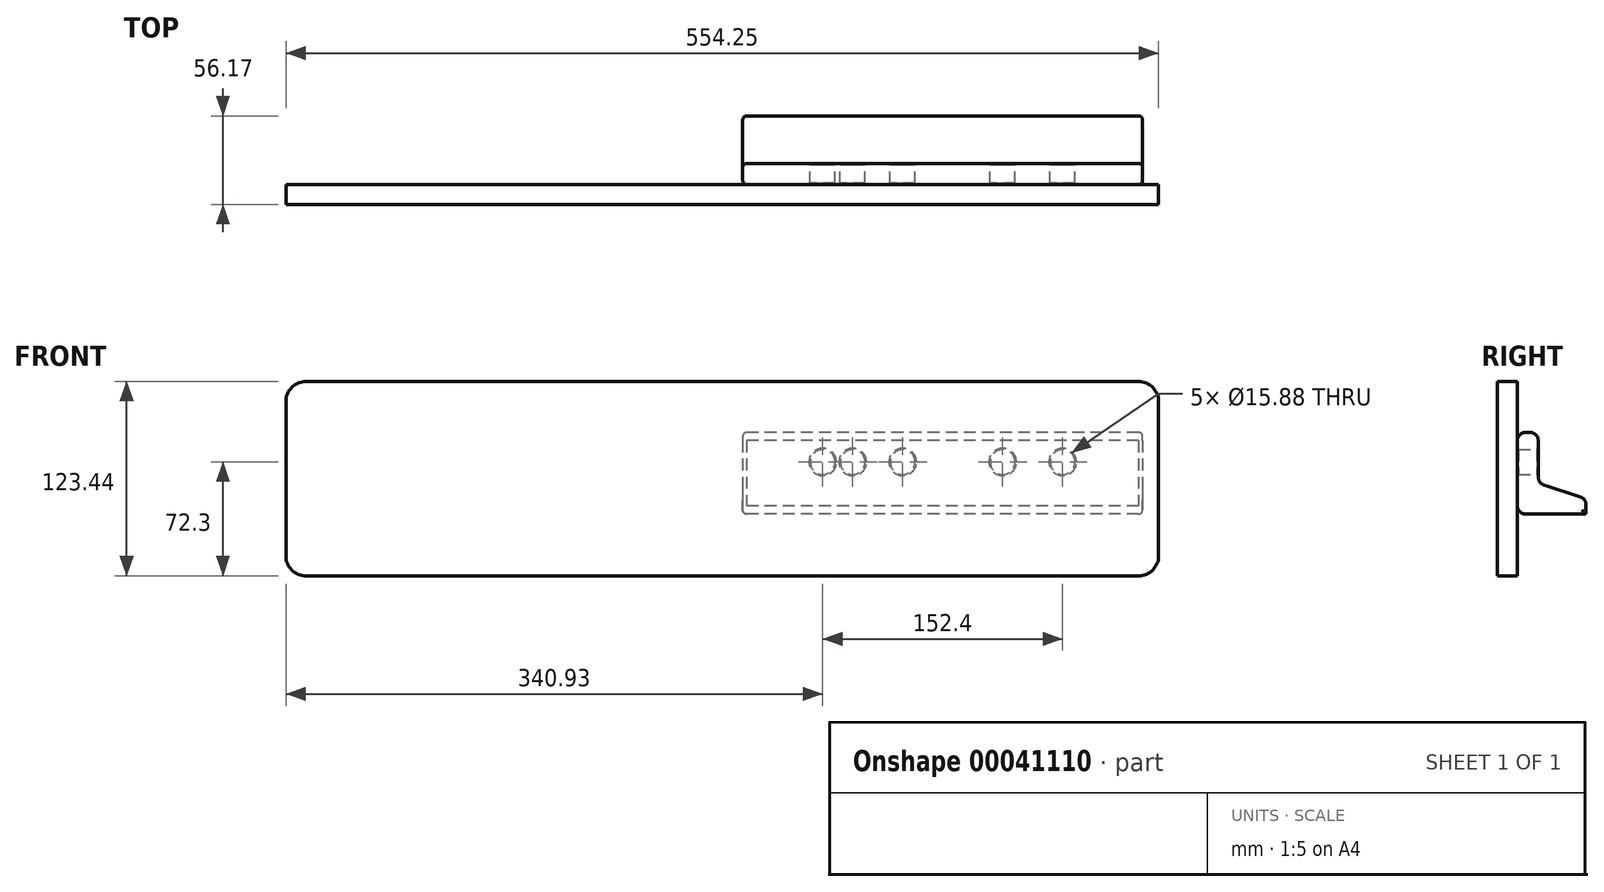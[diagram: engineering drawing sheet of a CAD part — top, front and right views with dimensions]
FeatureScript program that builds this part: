
annotation { "Feature Type Name" : "Feature", "Feature Type Description" : "" }
export const myFeature = defineFeature(function(context is Context, id is Id, definition is map)
    precondition{}
    {
        {
            var Q0;
            Q0=qCreatedBy(makeId("Right.planeOp"),FACE);
            var sketch = newSketch(context, id + "F0", { "sketchPlane" : qUnion([Q0])});
            skLineSegment(sketch, "E0.bottom", {"start": v(0, 51.75) * mm, "end": v(13.23, 51.75) * mm});
            skLineSegment(sketch, "E0.top", {"start": v(0, 0) * mm, "end": v(13.23, 0) * mm});
            skLineSegment(sketch, "E0.left", {"start": v(0, 51.75) * mm, "end": v(0, 0) * mm});
            skLineSegment(sketch, "E1.bottom", {"start": v(43.47, 0) * mm, "end": v(13.23, 0) * mm});
            skLineSegment(sketch, "E1.left", {"start": v(43.47, 0) * mm, "end": v(43.47, 9.81) * mm});
            skLineSegment(sketch, "E2", {"start": v(13.23, 51.75) * mm, "end": v(13.23, 19.71) * mm});
            skLineSegment(sketch, "E3", {"start": v(13.23, 19.71) * mm, "end": v(43.47, 9.81) * mm});
            skSolve(sketch);
        }
        {
            var Q0;
            Q0=makeQuery(id+"F0.imprint","IMPRINT",FACE,{"disambiguationData":[TD([[makeQuery(id+"F0.imprint","IMPRINT",EDGE,{"derivedFrom":sQuery(id+"F0.wireOp",EDGE,"E0.bottom")}),-1.0]])]});
            extrude(context, id + "F1", {"entities" : qUnion([Q0]), "depth" : 254 * mm, "symmetric" : true});
        }
        {
            var Q0;
            Q0=makeQuery(id+"F1.opExtrude","SWEPT_EDGE",EDGE,{"disambiguationData":[OSD([sQuery(id+"F0.wireOp",EDGE,"E0.bottom"),sQuery(id+"F0.wireOp",EDGE,"E0.left")])]});
            var Q1;
            Q1=makeQuery(id+"F1.opExtrude","SWEPT_EDGE",EDGE,{"disambiguationData":[OSD([sQuery(id+"F0.wireOp",EDGE,"E0.top"),sQuery(id+"F0.wireOp",EDGE,"E0.left")])]});
            var Q2;
            Q2=makeQuery(id+"F1.opExtrude","SWEPT_EDGE",EDGE,{"disambiguationData":[OSD([sQuery(id+"F0.wireOp",EDGE,"E1.left"),sQuery(id+"F0.wireOp",EDGE,"E3")])]});
            var Q3;
            Q3=makeQuery(id+"F1.opExtrude","SWEPT_EDGE",EDGE,{"disambiguationData":[OSD([sQuery(id+"F0.wireOp",EDGE,"E0.bottom"),sQuery(id+"F0.wireOp",EDGE,"E2")])]});
            var Q4;
            Q4=makeQuery(id+"F1.opExtrude","SWEPT_EDGE",EDGE,{"disambiguationData":[OSD([sQuery(id+"F0.wireOp",EDGE,"E2"),sQuery(id+"F0.wireOp",EDGE,"E3")])]});
            fillet(context, id + "F2", {"entities" : qUnion([Q0, Q1, Q2, Q3, Q4]), "radius" : 5.08 * mm, "tangentPropagation" : true, "allowEdgeOverflow" : false});
        }
        {
            var Q0;
            Q0=makeQuery(id+"F1.opExtrude","CAP_EDGE",EDGE,{"disambiguationData":[OSD([sQuery(id+"F0.wireOp",EDGE,"E0.left")])],"isStart":true});
            var Q1;
            Q1=makeQuery(id+"F1.opExtrude","CAP_EDGE",EDGE,{"disambiguationData":[OSD([sQuery(id+"F0.wireOp",EDGE,"E0.left")])],"isStart":false});
            fillet(context, id + "F3", {"entities" : qUnion([Q0, Q1]), "radius" : 2.54 * mm, "tangentPropagation" : true, "allowEdgeOverflow" : false});
        }
        {
            var Q0;
            Q0=makeQuery(id+"F1.opExtrude","SWEPT_FACE",FACE,{"disambiguationData":[OSD([sQuery(id+"F0.wireOp",EDGE,"E2")])]});
            var sketch = newSketch(context, id + "F4", { "sketchPlane" : qUnion([Q0])});
            skCircle(sketch, "E4", {"center": v(25.4, 33.02) * mm, "radius": 7.94 * mm});
            skCircle(sketch, "E5", {"center": v(57.15, 33.02) * mm, "radius": 7.94 * mm});
            skCircle(sketch, "E6", {"center": v(76.2, 33.02) * mm, "radius": 7.94 * mm});
            skCircle(sketch, "E7", {"center": v(-76.2, 33.02) * mm, "radius": 7.94 * mm});
            skCircle(sketch, "E8", {"center": v(-38.1, 33.02) * mm, "radius": 7.94 * mm});
            skSolve(sketch);
        }
        {
            var Q0;
            Q0=makeQuery(id+"F4.imprint","IMPRINT",FACE,{"disambiguationData":[TD([[makeQuery(id+"F4.imprint","IMPRINT",EDGE,{"derivedFrom":sQuery(id+"F4.wireOp",EDGE,"E7")}),1.0]])]});
            var Q1;
            Q1=makeQuery(id+"F4.imprint","IMPRINT",FACE,{"disambiguationData":[TD([[makeQuery(id+"F4.imprint","IMPRINT",EDGE,{"derivedFrom":sQuery(id+"F4.wireOp",EDGE,"E8")}),1.0]])]});
            var Q2;
            Q2=makeQuery(id+"F4.imprint","IMPRINT",FACE,{"disambiguationData":[TD([[makeQuery(id+"F4.imprint","IMPRINT",EDGE,{"derivedFrom":sQuery(id+"F4.wireOp",EDGE,"E4")}),1.0]])]});
            var Q3;
            Q3=makeQuery(id+"F4.imprint","IMPRINT",FACE,{"disambiguationData":[TD([[makeQuery(id+"F4.imprint","IMPRINT",EDGE,{"derivedFrom":sQuery(id+"F4.wireOp",EDGE,"E5")}),1.0]])]});
            var Q4;
            Q4=makeQuery(id+"F4.imprint","IMPRINT",FACE,{"disambiguationData":[TD([[makeQuery(id+"F4.imprint","IMPRINT",EDGE,{"derivedFrom":sQuery(id+"F4.wireOp",EDGE,"E6")}),1.0]])]});
            var Q5;
            Q5=makeQuery(id+"F1.opExtrude","SWEPT_FACE",FACE,{"disambiguationData":[OSD([sQuery(id+"F0.wireOp",EDGE,"E0.left")])]});
            extrude(context, id + "F5", {"entities" : qUnion([Q0, Q1, Q2, Q3, Q4]), "operationType" : NewBodyOperationType.REMOVE, "endBound" : BoundingType.UP_TO_SURFACE, "oppositeDirection" : true, "endBoundEntityFace" : qUnion([Q5]), "depth" : 25.4 * mm});
        }
        {
            var Q0;
            Q0=makeQuery(id+"F5.boolean.opBoolean","COPY",FACE,{"derivedFrom":makeQuery(id+"F5.opExtrude","SWEPT_FACE",FACE,{"disambiguationData":[OSD([sQuery(id+"F4.wireOp",EDGE,"E7")])]})});
            var Q1;
            Q1=makeQuery(id+"F5.boolean.opBoolean","COPY",FACE,{"derivedFrom":makeQuery(id+"F5.opExtrude","SWEPT_FACE",FACE,{"disambiguationData":[OSD([sQuery(id+"F4.wireOp",EDGE,"E8")])]})});
            var Q2;
            Q2=makeQuery(id+"F5.boolean.opBoolean","COPY",FACE,{"derivedFrom":makeQuery(id+"F5.opExtrude","SWEPT_FACE",FACE,{"disambiguationData":[OSD([sQuery(id+"F4.wireOp",EDGE,"E4")])]})});
            var Q3;
            Q3=makeQuery(id+"F5.boolean.opBoolean","COPY",FACE,{"derivedFrom":makeQuery(id+"F5.opExtrude","SWEPT_FACE",FACE,{"disambiguationData":[OSD([sQuery(id+"F4.wireOp",EDGE,"E5")])]})});
            var Q4;
            Q4=makeQuery(id+"F5.boolean.opBoolean","COPY",FACE,{"derivedFrom":makeQuery(id+"F5.opExtrude","SWEPT_FACE",FACE,{"disambiguationData":[OSD([sQuery(id+"F4.wireOp",EDGE,"E6")])]})});
            chamfer(context, id + "F6", {"entities" : qUnion([Q0, Q1, Q2, Q3, Q4]), "width" : 0.76 * mm, "tangentPropagation" : true});
        }
        {
            var Q0;
            Q0=qCreatedBy(makeId("Front.planeOp"),FACE);
            var sketch = newSketch(context, id + "F7", { "sketchPlane" : qUnion([Q0])});
            skLineSegment(sketch, "E9.bottom", {"start": v(124.42, 84.16) * mm, "end": v(-140, 84.16) * mm});
            skLineSegment(sketch, "E9.top", {"start": v(124.42, -39.28) * mm, "end": v(-140, -39.28) * mm});
            skLineSegment(sketch, "E9.left", {"start": v(137.12, 71.46) * mm, "end": v(137.12, -26.58) * mm});
            skLineSegment(sketch, "E9.right", {"start": v(-140, 84.16) * mm, "end": v(-140, -39.28) * mm});
            skPoint(sketch, "E10.visualSharp", {"position": v(-140, 84.16) * mm});
            skPoint(sketch, "E11.visualSharp", {"position": v(-140, -39.28) * mm});
            skPoint(sketch, "E12.visualSharp", {"position": v(137.12, -39.28) * mm});
            skArc(sketch, "E12.filletArc", {"start": v(124.42, -39.28) * mm, "mid": v(133.4, -35.56) * mm, "end": v(137.12, -26.58) * mm});
            skPoint(sketch, "E13.visualSharp", {"position": v(137.12, 84.16) * mm});
            skArc(sketch, "E13.filletArc", {"start": v(137.12, 71.46) * mm, "mid": v(133.4, 80.44) * mm, "end": v(124.42, 84.16) * mm});
            skSolve(sketch);
        }
        {
            var Q0;
            Q0=makeQuery(id+"F7.imprint","IMPRINT",FACE,{"disambiguationData":[TD([[makeQuery(id+"F7.imprint","IMPRINT",EDGE,{"derivedFrom":sQuery(id+"F7.wireOp",EDGE,"E9.bottom")}),1.0]])]});
            extrude(context, id + "F8", {"entities" : qUnion([Q0]), "offsetDistance" : 25.4 * mm, "depth" : 12.7 * mm});
        }
        {
            var Q0;
            Q0=makeQuery(id+"F8.opExtrude","SWEPT_BODY",BODY,{"disambiguationData":[OSD([sQuery(id+"F7.wireOp",EDGE,"E9.bottom"),sQuery(id+"F7.wireOp",EDGE,"E9.top"),sQuery(id+"F7.wireOp",EDGE,"E9.left"),sQuery(id+"F7.wireOp",EDGE,"E9.right"),sQuery(id+"F7.wireOp",EDGE,"E12.filletArc"),sQuery(id+"F7.wireOp",EDGE,"E13.filletArc")])]});
            var Q1;
            Q1=makeQuery(id+"F8.opExtrude","SWEPT_FACE",FACE,{"disambiguationData":[OSD([sQuery(id+"F7.wireOp",EDGE,"E9.right")])]});
            mirror(context, id + "F9", {"operationType" : NewBodyOperationType.ADD, "entities" : qUnion([Q0]), "mirrorPlane" : qUnion([Q1])});
        }
    });
